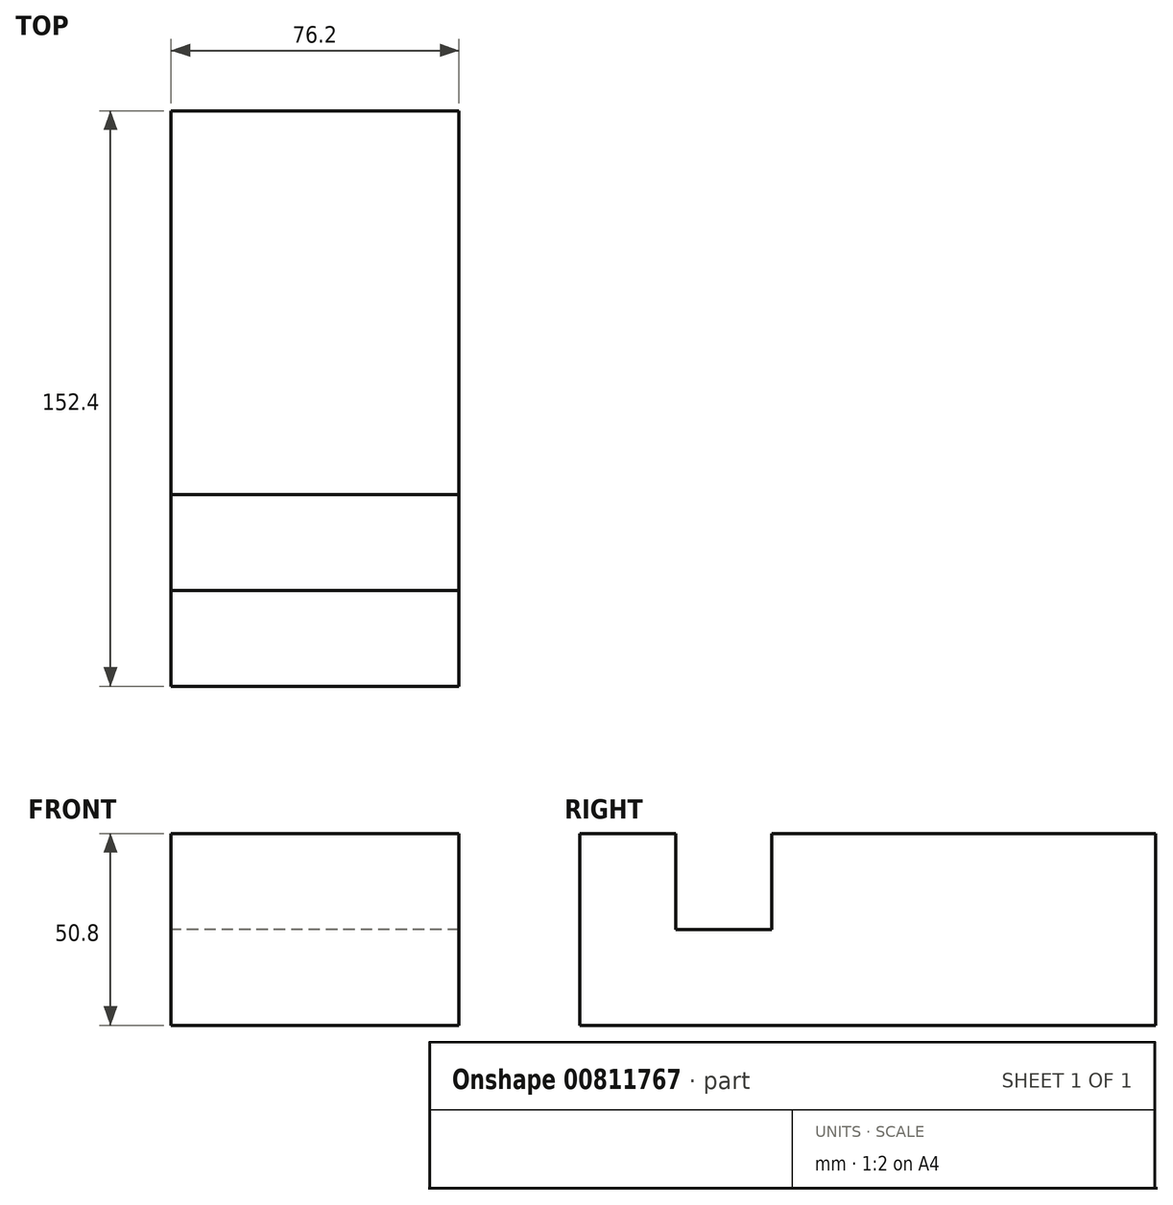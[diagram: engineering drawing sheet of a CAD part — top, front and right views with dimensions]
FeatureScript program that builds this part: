
annotation { "Feature Type Name" : "Feature", "Feature Type Description" : "" }
export const myFeature = defineFeature(function(context is Context, id is Id, definition is map)
    precondition{}
    {
        {
            var Q0;
            Q0=qCreatedBy(makeId("Right.planeOp"),FACE);
            var sketch = newSketch(context, id + "F0", { "sketchPlane" : qUnion([Q0])});
            skLineSegment(sketch, "E0", {"start": v(0, 0) * mm, "end": v(0, 50.8) * mm});
            skLineSegment(sketch, "E1", {"start": v(0, 0) * mm, "end": v(-152.4, 0) * mm});
            skLineSegment(sketch, "E2", {"start": v(-152.4, 0) * mm, "end": v(-152.4, 50.8) * mm});
            skLineSegment(sketch, "E3", {"start": v(0, 50.8) * mm, "end": v(-101.6, 50.8) * mm});
            skLineSegment(sketch, "E4", {"start": v(-152.4, 50.8) * mm, "end": v(-127, 50.8) * mm});
            skLineSegment(sketch, "E5", {"start": v(-127, 50.8) * mm, "end": v(-127, 25.4) * mm});
            skLineSegment(sketch, "E6", {"start": v(-127, 25.4) * mm, "end": v(-101.6, 25.4) * mm});
            skLineSegment(sketch, "E7", {"start": v(-101.6, 25.4) * mm, "end": v(-101.6, 50.8) * mm});
            skSolve(sketch);
        }
        {
            var Q0;
            Q0=makeQuery(id+"F0.imprint","IMPRINT",FACE,{"disambiguationData":[TD([[makeQuery(id+"F0.imprint","IMPRINT",EDGE,{"derivedFrom":sQuery(id+"F0.wireOp",EDGE,"E0")}),1.0]])]});
            extrude(context, id + "F1", {"entities" : qUnion([Q0]), "depth" : 76.2 * mm, "offsetDistance" : 25.4 * mm});
        }
    });
